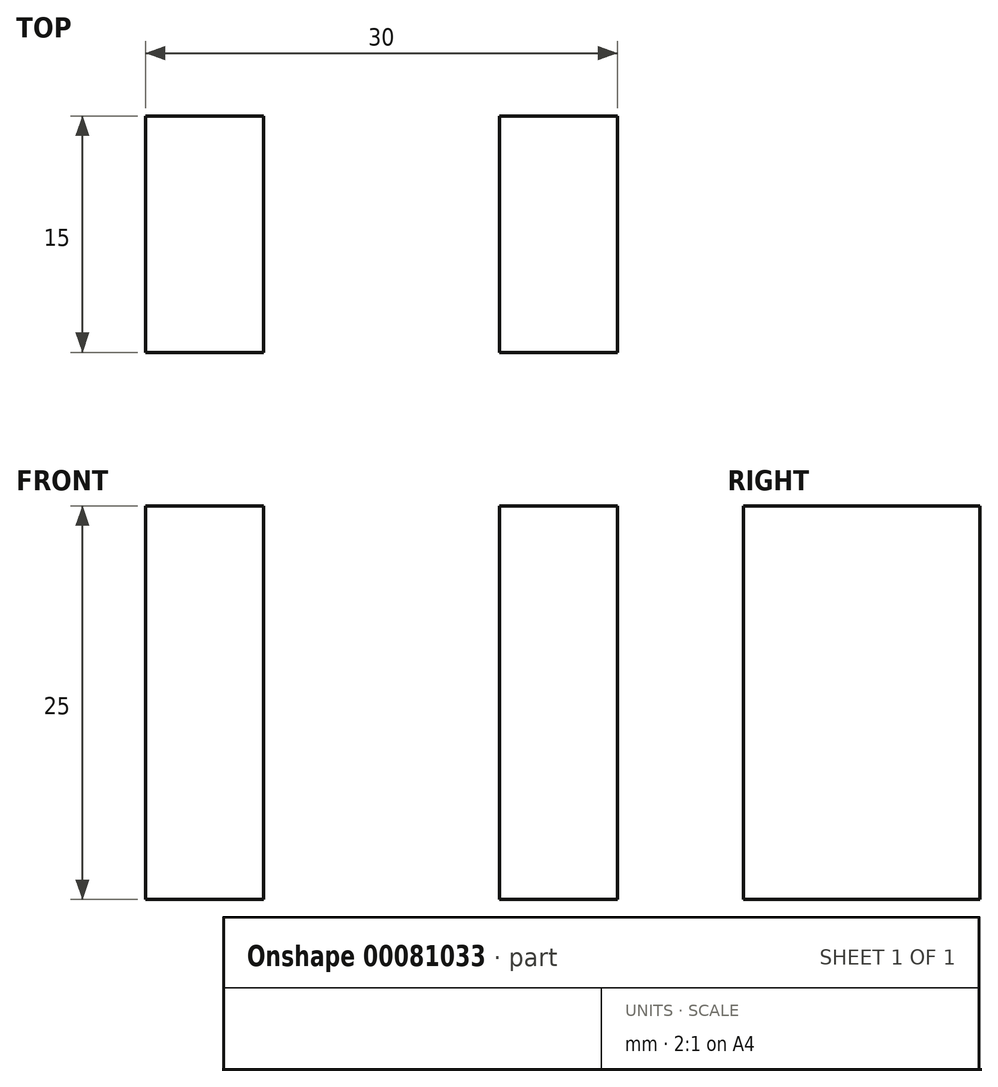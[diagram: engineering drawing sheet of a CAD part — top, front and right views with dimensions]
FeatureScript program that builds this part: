
annotation { "Feature Type Name" : "Feature", "Feature Type Description" : "" }
export const myFeature = defineFeature(function(context is Context, id is Id, definition is map)
    precondition{}
    {
        {
            var Q0;
            Q0=qCreatedBy(makeId("Top.planeOp"),FACE);
            var sketch = newSketch(context, id + "F0", { "sketchPlane" : qUnion([Q0])});
            skLineSegment(sketch, "E0.bottom", {"start": v(0, 0) * mm, "end": v(30, 0) * mm});
            skLineSegment(sketch, "E0.top", {"start": v(0, 15) * mm, "end": v(30, 15) * mm});
            skLineSegment(sketch, "E0.left", {"start": v(0, 0) * mm, "end": v(0, 15) * mm});
            skLineSegment(sketch, "E0.right", {"start": v(30, 0) * mm, "end": v(30, 15) * mm});
            skLineSegment(sketch, "E1", {"start": v(7.5, 7.5) * mm, "end": v(7.5, 15) * mm});
            skLineSegment(sketch, "E2", {"start": v(7.5, 7.5) * mm, "end": v(7.5, 0) * mm});
            skLineSegment(sketch, "E3", {"start": v(22.5, 7.5) * mm, "end": v(22.5, 15) * mm});
            skLineSegment(sketch, "E4", {"start": v(22.5, 7.5) * mm, "end": v(22.5, 0) * mm});
            skPoint(sketch, "E5.end.orphan", {"position": v(0, 7.5) * mm});
            skPoint(sketch, "E6.orphan", {"position": v(15, 7.5) * mm});
            skPoint(sketch, "E7.orphan", {"position": v(15, 0) * mm});
            skPoint(sketch, "E8.end.orphan", {"position": v(15, 15) * mm});
            skPoint(sketch, "E9.end.orphan", {"position": v(30, 7.5) * mm});
            skSolve(sketch);
        }
        {
            var Q0;
            {var subQ1=sQuery(id+"F0.wireOp",EDGE,"E0.left");Q0=makeQuery(id+"F0.imprint","IMPRINT",FACE,{"disambiguationData":[TD([[makeQuery(id+"F0.imprint","IMPRINT",EDGE,{"derivedFrom":subQ1}),-1.0]])]});}
            var Q1;
            {var subQ1=sQuery(id+"F0.wireOp",EDGE,"E0.right");Q1=makeQuery(id+"F0.imprint","IMPRINT",FACE,{"disambiguationData":[TD([[makeQuery(id+"F0.imprint","IMPRINT",EDGE,{"derivedFrom":subQ1}),1.0]])]});}
            extrude(context, id + "F1", {"entities" : qUnion([Q0, Q1]), "depth" : 25 * mm});
        }
    });
